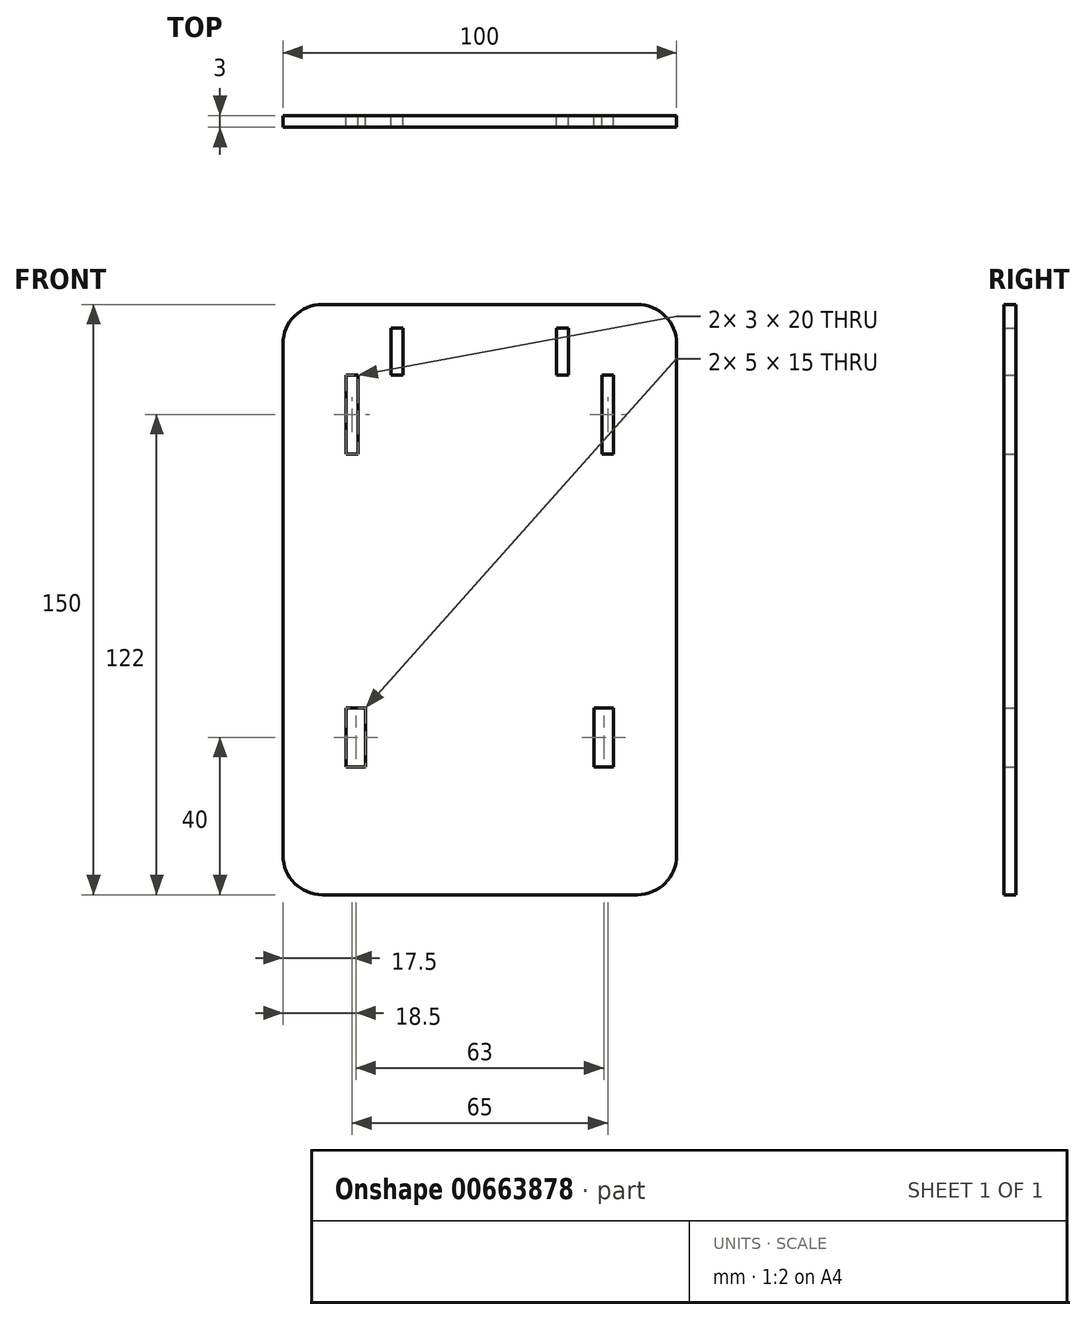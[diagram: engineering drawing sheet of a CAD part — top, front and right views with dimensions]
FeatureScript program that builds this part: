
annotation { "Feature Type Name" : "Feature", "Feature Type Description" : "" }
export const myFeature = defineFeature(function(context is Context, id is Id, definition is map)
    precondition{}
    {
        {
            var Q0;
            Q0=qCreatedBy(makeId("Front.planeOp"),FACE);
            var sketch = newSketch(context, id + "F0", { "sketchPlane" : qUnion([Q0])});
            skLineSegment(sketch, "E0.bottom", {"start": v(40, 75) * mm, "end": v(-40, 75) * mm});
            skLineSegment(sketch, "E0.top", {"start": v(40, -75) * mm, "end": v(-40, -75) * mm});
            skLineSegment(sketch, "E0.left", {"start": v(50, 65) * mm, "end": v(50, -65) * mm});
            skLineSegment(sketch, "E0.right", {"start": v(-50, 65) * mm, "end": v(-50, -65) * mm});
            skPoint(sketch, "E0.middle", {"position": v(0, 0) * mm});
            skLineSegment(sketch, "E1.bottom", {"start": v(19.5, 69) * mm, "end": v(22.5, 69) * mm});
            skLineSegment(sketch, "E1.top", {"start": v(19.5, 57) * mm, "end": v(22.5, 57) * mm});
            skLineSegment(sketch, "E1.left", {"start": v(19.5, 69) * mm, "end": v(19.5, 57) * mm});
            skLineSegment(sketch, "E1.right", {"start": v(22.5, 69) * mm, "end": v(22.5, 57) * mm});
            skLineSegment(sketch, "E2.bottom", {"start": v(31, 57) * mm, "end": v(34, 57) * mm});
            skLineSegment(sketch, "E2.top", {"start": v(31, 37) * mm, "end": v(34, 37) * mm});
            skLineSegment(sketch, "E2.left", {"start": v(31, 57) * mm, "end": v(31, 37) * mm});
            skLineSegment(sketch, "E2.right", {"start": v(34, 57) * mm, "end": v(34, 37) * mm});
            skLineSegment(sketch, "E3.bottom", {"start": v(29, -27.5) * mm, "end": v(34, -27.5) * mm});
            skLineSegment(sketch, "E3.top", {"start": v(29, -42.5) * mm, "end": v(34, -42.5) * mm});
            skLineSegment(sketch, "E3.left", {"start": v(29, -27.5) * mm, "end": v(29, -42.5) * mm});
            skLineSegment(sketch, "E3.right", {"start": v(34, -27.5) * mm, "end": v(34, -42.5) * mm});
            skPoint(sketch, "E4.visualSharp", {"position": v(-50, 75) * mm});
            skArc(sketch, "E4.filletArc", {"start": v(-40, 75) * mm, "mid": v(-47.07, 72.07) * mm, "end": v(-50, 65) * mm});
            skPoint(sketch, "E5.visualSharp", {"position": v(-50, -75) * mm});
            skArc(sketch, "E5.filletArc", {"start": v(-50, -65) * mm, "mid": v(-47.07, -72.07) * mm, "end": v(-40, -75) * mm});
            skPoint(sketch, "E6.visualSharp", {"position": v(50, -75) * mm});
            skArc(sketch, "E6.filletArc", {"start": v(40, -75) * mm, "mid": v(47.07, -72.07) * mm, "end": v(50, -65) * mm});
            skPoint(sketch, "E7.visualSharp", {"position": v(50, 75) * mm});
            skArc(sketch, "E7.filletArc", {"start": v(50, 65) * mm, "mid": v(47.07, 72.07) * mm, "end": v(40, 75) * mm});
            skLineSegment(sketch, "E8.MirrorCS", {"start": v(-29, -27.5) * mm, "end": v(-34, -27.5) * mm});
            skLineSegment(sketch, "E9.MirrorCS", {"start": v(-31, 37) * mm, "end": v(-34, 37) * mm});
            skLineSegment(sketch, "E10.MirrorCS", {"start": v(-31, 57) * mm, "end": v(-34, 57) * mm});
            skLineSegment(sketch, "E11.MirrorCS", {"start": v(-29, -42.5) * mm, "end": v(-34, -42.5) * mm});
            skLineSegment(sketch, "E12.MirrorCS", {"start": v(-19.5, 57) * mm, "end": v(-22.5, 57) * mm});
            skLineSegment(sketch, "E13.MirrorCS", {"start": v(-19.5, 69) * mm, "end": v(-22.5, 69) * mm});
            skLineSegment(sketch, "E14.MirrorCS", {"start": v(-34, 57) * mm, "end": v(-34, 37) * mm});
            skLineSegment(sketch, "E15.MirrorCS", {"start": v(-31, 57) * mm, "end": v(-31, 37) * mm});
            skLineSegment(sketch, "E16.MirrorCS", {"start": v(-22.5, 69) * mm, "end": v(-22.5, 57) * mm});
            skLineSegment(sketch, "E17.MirrorCS", {"start": v(-19.5, 69) * mm, "end": v(-19.5, 57) * mm});
            skLineSegment(sketch, "E18.MirrorCS", {"start": v(-34, -27.5) * mm, "end": v(-34, -42.5) * mm});
            skLineSegment(sketch, "E19.MirrorCS", {"start": v(-29, -27.5) * mm, "end": v(-29, -42.5) * mm});
            skSolve(sketch);
        }
        {
            var Q0;
            Q0 = qSketchRegion(id + "F0", true);
            extrude(context, id + "F1", {"entities" : qUnion([Q0]), "depth" : 3 * mm, "offsetDistance" : 25 * mm});
        }
    });
